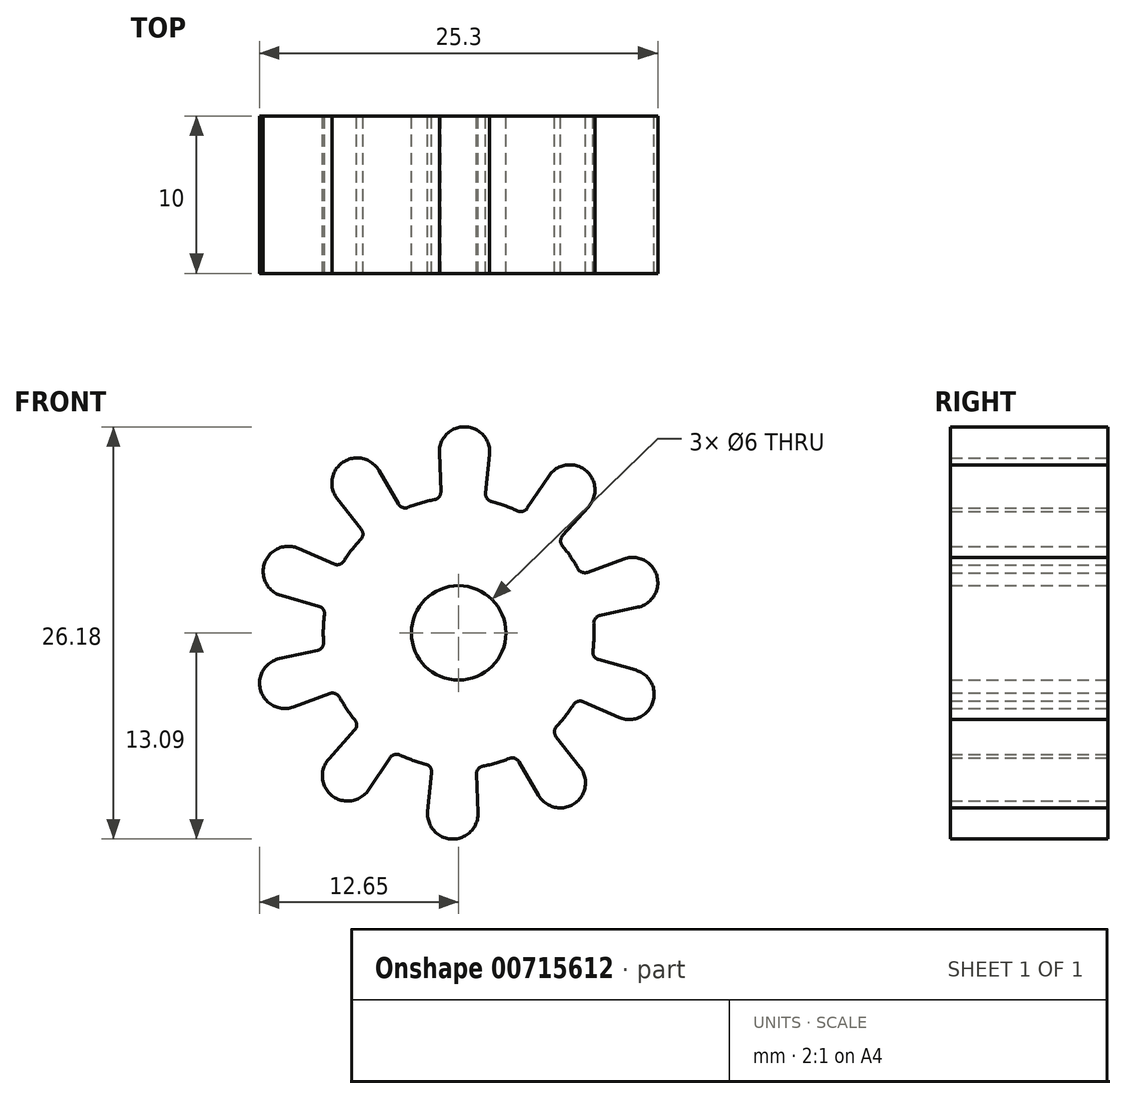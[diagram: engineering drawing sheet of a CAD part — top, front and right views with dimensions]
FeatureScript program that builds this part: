
annotation { "Feature Type Name" : "Feature", "Feature Type Description" : "" }
export const myFeature = defineFeature(function(context is Context, id is Id, definition is map)
    precondition{}
    {
        {
            var Q0;
            Q0=qCreatedBy(makeId("Front.planeOp"),FACE);
            var sketch = newSketch(context, id + "F0", { "sketchPlane" : qUnion([Q0])});
            skCircle(sketch, "E0", {"center": v(0, 0) * mm, "radius": 3 * mm});
            skCircle(sketch, "E1", {"center": v(0, 0) * mm, "radius": 8.6 * mm});
            skCircle(sketch, "E2", {"center": v(0, 0) * mm, "radius": 11.5 * mm, "construction": true});
            skCircle(sketch, "E3", {"center": v(0.37, 11.5) * mm, "radius": 1.6 * mm});
            skLineSegment(sketch, "E4", {"start": v(1.96, 11.33) * mm, "end": v(1.71, 8.88) * mm});
            skLineSegment(sketch, "E5", {"start": v(-1.23, 11.43) * mm, "end": v(-1.14, 8.97) * mm});
            skArc(sketch, "E6", {"start": v(-1.55, 8.46) * mm, "mid": v(-1.25, 8.64) * mm, "end": v(-1.14, 8.97) * mm});
            skArc(sketch, "E7", {"start": v(1.71, 8.88) * mm, "mid": v(1.8, 8.54) * mm, "end": v(2.09, 8.34) * mm});
            skCircle(sketch, "E8.1.0", {"center": v(-6.46, 9.52) * mm, "radius": 1.6 * mm});
            skLineSegment(sketch, "E8.1.1", {"start": v(-5.07, 10.32) * mm, "end": v(-3.83, 8.19) * mm});
            skArc(sketch, "E8.1.2", {"start": v(-3.83, 8.19) * mm, "mid": v(-3.56, 7.97) * mm, "end": v(-3.21, 7.98) * mm});
            skLineSegment(sketch, "E8.1.3", {"start": v(-7.71, 8.53) * mm, "end": v(-6.2, 6.6) * mm});
            skArc(sketch, "E8.1.4", {"start": v(-6.22, 5.94) * mm, "mid": v(-6.09, 6.26) * mm, "end": v(-6.2, 6.6) * mm});
            skCircle(sketch, "E8.2.0", {"center": v(-10.82, 3.9) * mm, "radius": 1.6 * mm});
            skLineSegment(sketch, "E8.2.1", {"start": v(-10.17, 5.37) * mm, "end": v(-7.91, 4.37) * mm});
            skArc(sketch, "E8.2.2", {"start": v(-7.91, 4.37) * mm, "mid": v(-7.57, 4.35) * mm, "end": v(-7.29, 4.56) * mm});
            skLineSegment(sketch, "E8.2.3", {"start": v(-11.25, 2.37) * mm, "end": v(-8.88, 1.7) * mm});
            skArc(sketch, "E8.2.4", {"start": v(-8.52, 1.14) * mm, "mid": v(-8.6, 1.49) * mm, "end": v(-8.88, 1.7) * mm});
            skCircle(sketch, "E9.1.3.0", {"center": v(-11.05, -3.2) * mm, "radius": 1.6 * mm});
            skLineSegment(sketch, "E9.2.3.0", {"start": v(-11.38, -1.63) * mm, "end": v(-8.97, -1.11) * mm});
            skArc(sketch, "E9.5.3.0", {"start": v(-8.97, -1.11) * mm, "mid": v(-8.68, -0.93) * mm, "end": v(-8.58, -0.6) * mm});
            skLineSegment(sketch, "E9.9.3.0", {"start": v(-10.5, -4.7) * mm, "end": v(-8.18, -3.85) * mm});
            skArc(sketch, "E9.12.3.0", {"start": v(-7.57, -4.08) * mm, "mid": v(-7.83, -3.85) * mm, "end": v(-8.18, -3.85) * mm});
            skCircle(sketch, "E9.1.4.0", {"center": v(-7.06, -9.08) * mm, "radius": 1.6 * mm});
            skLineSegment(sketch, "E9.2.4.0", {"start": v(-8.25, -8.01) * mm, "end": v(-6.6, -6.18) * mm});
            skArc(sketch, "E9.5.4.0", {"start": v(-6.6, -6.18) * mm, "mid": v(-6.48, -5.85) * mm, "end": v(-6.6, -5.52) * mm});
            skLineSegment(sketch, "E9.9.4.0", {"start": v(-5.73, -9.97) * mm, "end": v(-4.35, -7.92) * mm});
            skArc(sketch, "E9.12.4.0", {"start": v(-3.72, -7.75) * mm, "mid": v(-4.07, -7.72) * mm, "end": v(-4.35, -7.92) * mm});
            skCircle(sketch, "E9.1.5.0", {"center": v(-0.37, -11.5) * mm, "radius": 1.6 * mm});
            skLineSegment(sketch, "E9.2.5.0", {"start": v(-1.96, -11.33) * mm, "end": v(-1.71, -8.88) * mm});
            skArc(sketch, "E9.5.5.0", {"start": v(-1.71, -8.88) * mm, "mid": v(-1.8, -8.54) * mm, "end": v(-2.09, -8.34) * mm});
            skLineSegment(sketch, "E9.9.5.0", {"start": v(1.23, -11.43) * mm, "end": v(1.14, -8.97) * mm});
            skArc(sketch, "E9.12.5.0", {"start": v(1.55, -8.46) * mm, "mid": v(1.25, -8.64) * mm, "end": v(1.14, -8.97) * mm});
            skCircle(sketch, "E9.1.6.0", {"center": v(6.46, -9.52) * mm, "radius": 1.6 * mm});
            skLineSegment(sketch, "E9.2.6.0", {"start": v(5.07, -10.32) * mm, "end": v(3.83, -8.19) * mm});
            skArc(sketch, "E9.5.6.0", {"start": v(3.83, -8.19) * mm, "mid": v(3.56, -7.97) * mm, "end": v(3.21, -7.98) * mm});
            skLineSegment(sketch, "E9.9.6.0", {"start": v(7.71, -8.53) * mm, "end": v(6.2, -6.6) * mm});
            skArc(sketch, "E9.12.6.0", {"start": v(6.22, -5.94) * mm, "mid": v(6.09, -6.26) * mm, "end": v(6.2, -6.6) * mm});
            skCircle(sketch, "E9.1.7.0", {"center": v(10.82, -3.9) * mm, "radius": 1.6 * mm});
            skLineSegment(sketch, "E9.2.7.0", {"start": v(10.17, -5.37) * mm, "end": v(7.91, -4.37) * mm});
            skArc(sketch, "E9.5.7.0", {"start": v(7.91, -4.37) * mm, "mid": v(7.57, -4.35) * mm, "end": v(7.29, -4.56) * mm});
            skLineSegment(sketch, "E9.9.7.0", {"start": v(11.25, -2.37) * mm, "end": v(8.88, -1.7) * mm});
            skArc(sketch, "E9.12.7.0", {"start": v(8.52, -1.14) * mm, "mid": v(8.6, -1.49) * mm, "end": v(8.88, -1.7) * mm});
            skCircle(sketch, "E9.1.8.0", {"center": v(11.05, 3.2) * mm, "radius": 1.6 * mm});
            skLineSegment(sketch, "E9.2.8.0", {"start": v(11.38, 1.63) * mm, "end": v(8.97, 1.11) * mm});
            skArc(sketch, "E9.5.8.0", {"start": v(8.97, 1.11) * mm, "mid": v(8.68, 0.93) * mm, "end": v(8.58, 0.6) * mm});
            skLineSegment(sketch, "E9.9.8.0", {"start": v(10.5, 4.7) * mm, "end": v(8.18, 3.85) * mm});
            skArc(sketch, "E9.12.8.0", {"start": v(7.57, 4.08) * mm, "mid": v(7.83, 3.85) * mm, "end": v(8.18, 3.85) * mm});
            skCircle(sketch, "E9.1.9.0", {"center": v(7.06, 9.08) * mm, "radius": 1.6 * mm});
            skLineSegment(sketch, "E9.2.9.0", {"start": v(8.25, 8.01) * mm, "end": v(6.6, 6.18) * mm});
            skArc(sketch, "E9.5.9.0", {"start": v(6.6, 6.18) * mm, "mid": v(6.48, 5.85) * mm, "end": v(6.6, 5.52) * mm});
            skLineSegment(sketch, "E9.9.9.0", {"start": v(5.73, 9.97) * mm, "end": v(4.35, 7.92) * mm});
            skArc(sketch, "E9.12.9.0", {"start": v(3.72, 7.75) * mm, "mid": v(4.07, 7.72) * mm, "end": v(4.35, 7.92) * mm});
            skSolve(sketch);
        }
        {
            var Q0;
            Q0 = qSketchRegion(id + "F0", true);
            extrude(context, id + "F1", {"entities" : qUnion([Q0]), "depth" : 10 * mm, "offsetDistance" : 25 * mm});
        }
    });
